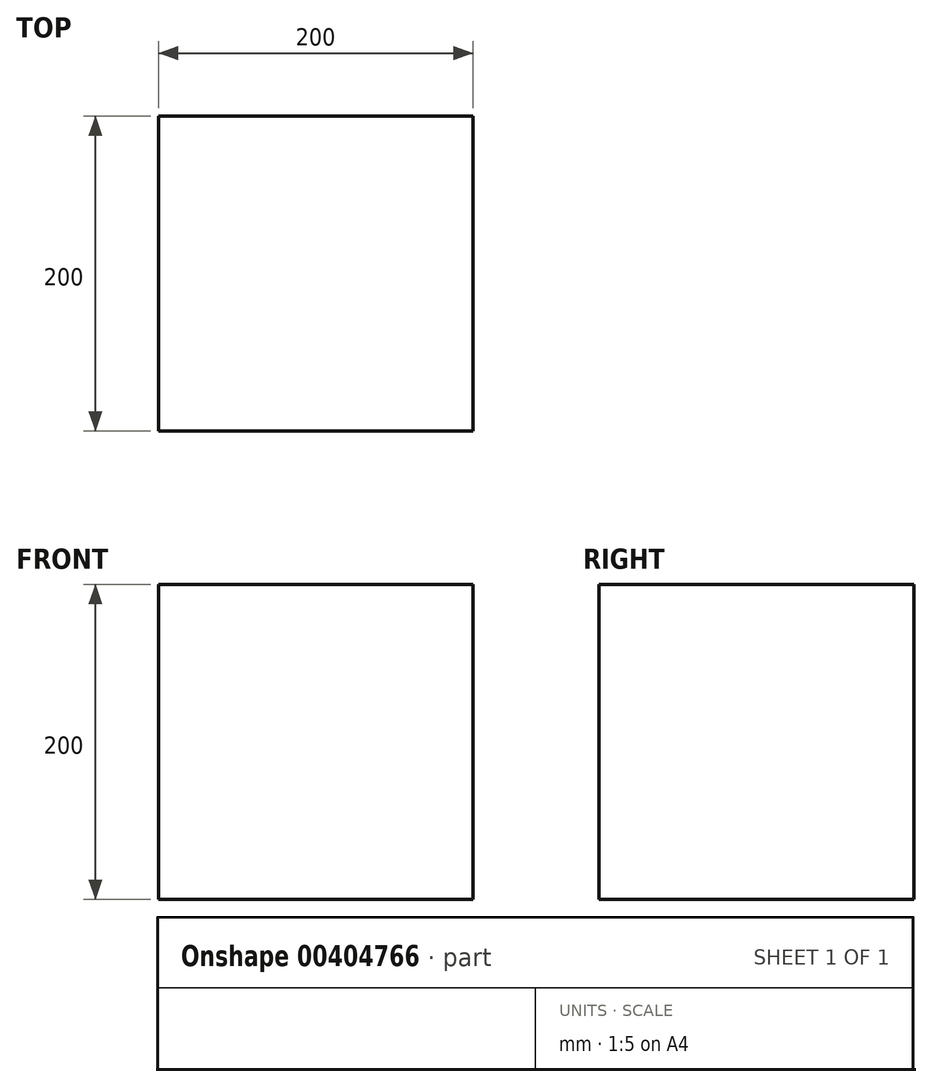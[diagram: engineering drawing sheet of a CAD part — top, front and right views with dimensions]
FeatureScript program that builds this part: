
annotation { "Feature Type Name" : "Feature", "Feature Type Description" : "" }
export const myFeature = defineFeature(function(context is Context, id is Id, definition is map)
    precondition{}
    {
        {
            var Q0;
            Q0=qCreatedBy(makeId("Front.planeOp"),FACE);
            var sketch = newSketch(context, id + "F0", { "sketchPlane" : qUnion([Q0])});
            skPoint(sketch, "E0.middle", {"position": v(0, 0) * mm});
            skLineSegment(sketch, "E1.bottom", {"start": v(-100, 100) * mm, "end": v(100, 100) * mm});
            skLineSegment(sketch, "E1.top", {"start": v(-100, -100) * mm, "end": v(100, -100) * mm});
            skLineSegment(sketch, "E1.left", {"start": v(-100, 100) * mm, "end": v(-100, -100) * mm});
            skLineSegment(sketch, "E1.right", {"start": v(100, 100) * mm, "end": v(100, -100) * mm});
            skLineSegment(sketch, "E2", {"start": v(0, 100) * mm, "end": v(100, 0) * mm});
            skSolve(sketch);
        }
        {
            var Q0;
            Q0=makeQuery(id+"F0.imprint","IMPRINT",FACE,{"disambiguationData":[TD([[makeQuery(id+"F0.imprint","IMPRINT",EDGE,{"derivedFrom":sQuery(id+"F0.wireOp",EDGE,"E1.bottom")}),-1.0]])]});
            extrude(context, id + "F1", {"entities" : qUnion([Q0]), "depth" : 200 * mm});
        }
        {
            var Q0;
            {var subQ1=sQuery(id+"F0.wireOp",EDGE,"E1.top");Q0=makeQuery(id+"F0.imprint","IMPRINT",FACE,{"disambiguationData":[TD([[makeQuery(id+"F0.imprint","IMPRINT",EDGE,{"derivedFrom":subQ1}),1.0]])]});}
            extrude(context, id + "F2", {"entities" : qUnion([Q0]), "operationType" : NewBodyOperationType.ADD, "depth" : 200 * mm});
        }
    });
